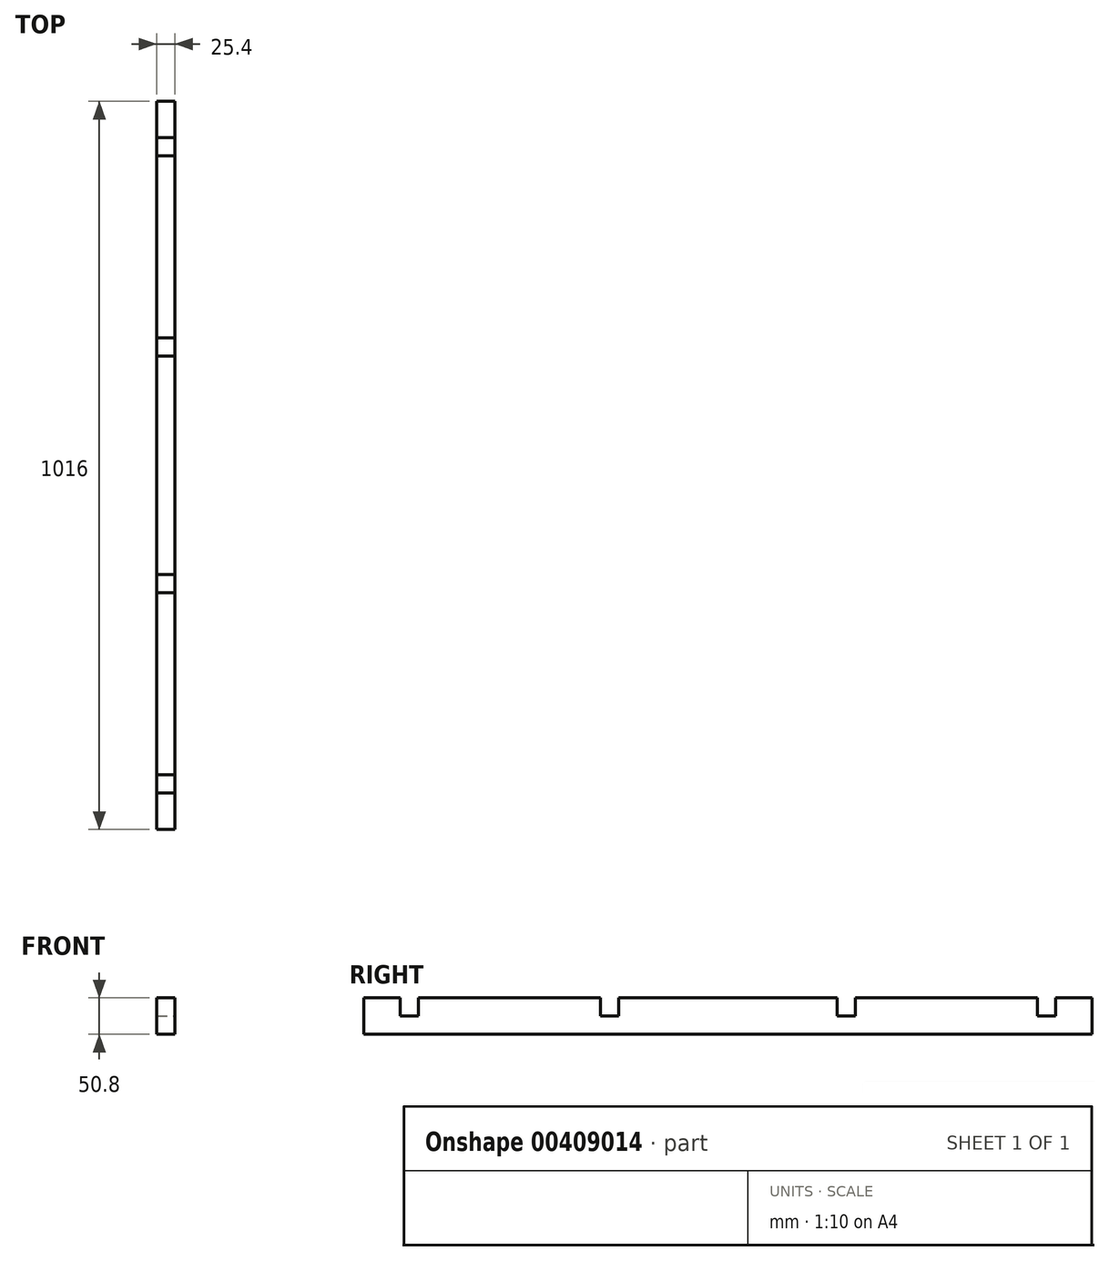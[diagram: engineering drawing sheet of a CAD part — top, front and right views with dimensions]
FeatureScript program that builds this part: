
annotation { "Feature Type Name" : "Feature", "Feature Type Description" : "" }
export const myFeature = defineFeature(function(context is Context, id is Id, definition is map)
    precondition{}
    {
        {
            var Q0;
            Q0=qCreatedBy(makeId("Right.planeOp"),FACE);
            var sketch = newSketch(context, id + "F0", { "sketchPlane" : qUnion([Q0])});
            skLineSegment(sketch, "E0.bottom", {"start": v(-508, 25.4) * mm, "end": v(508, 25.4) * mm});
            skLineSegment(sketch, "E0.top", {"start": v(-508, -25.4) * mm, "end": v(508, -25.4) * mm});
            skLineSegment(sketch, "E0.left", {"start": v(-508, 25.4) * mm, "end": v(-508, -25.4) * mm});
            skLineSegment(sketch, "E0.right", {"start": v(508, 25.4) * mm, "end": v(508, -25.4) * mm});
            skPoint(sketch, "E0.middle", {"position": v(0, 0) * mm});
            skSolve(sketch);
        }
        {
            var Q0;
            Q0=makeQuery(id+"F0.imprint","IMPRINT",FACE,{"disambiguationData":[TD([[makeQuery(id+"F0.imprint","IMPRINT",EDGE,{"derivedFrom":sQuery(id+"F0.wireOp",EDGE,"E0.bottom")}),-1.0]])]});
            extrude(context, id + "F1", {"entities" : qUnion([Q0]), "depth" : 25.4 * mm});
        }
        {
            var Q0;
            Q0=makeQuery(id+"F1.opExtrude","CAP_FACE",FACE,{"disambiguationData":[OSD([sQuery(id+"F0.wireOp",EDGE,"E0.bottom"),sQuery(id+"F0.wireOp",EDGE,"E0.top"),sQuery(id+"F0.wireOp",EDGE,"E0.left"),sQuery(id+"F0.wireOp",EDGE,"E0.right")])],"isStart":false});
            var sketch = newSketch(context, id + "F2", { "sketchPlane" : qUnion([Q0])});
            skLineSegment(sketch, "E1.bottom", {"start": v(-152.4, 0) * mm, "end": v(-177.8, 0) * mm});
            skLineSegment(sketch, "E1.top", {"start": v(-152.4, 25.4) * mm, "end": v(-177.8, 25.4) * mm});
            skLineSegment(sketch, "E1.left", {"start": v(-152.4, 0) * mm, "end": v(-152.4, 25.4) * mm});
            skLineSegment(sketch, "E1.right", {"start": v(-177.8, 0) * mm, "end": v(-177.8, 25.4) * mm});
            skLineSegment(sketch, "E2.bottom", {"start": v(152.4, 0) * mm, "end": v(177.8, 0) * mm});
            skLineSegment(sketch, "E2.top", {"start": v(152.4, 25.4) * mm, "end": v(177.8, 25.4) * mm});
            skLineSegment(sketch, "E2.left", {"start": v(152.4, 0) * mm, "end": v(152.4, 25.4) * mm});
            skLineSegment(sketch, "E2.right", {"start": v(177.8, 0) * mm, "end": v(177.8, 25.4) * mm});
            skSolve(sketch);
        }
        {
            var Q0;
            Q0 = qSketchRegion(id + "F2", true);
            extrude(context, id + "F3", {"entities" : qUnion([Q0]), "operationType" : NewBodyOperationType.REMOVE, "oppositeDirection" : true, "depth" : 25.4 * mm});
        }
        {
            var Q0;
            Q0=makeQuery(id+"F1.opExtrude","CAP_FACE",FACE,{"disambiguationData":[OSD([sQuery(id+"F0.wireOp",EDGE,"E0.bottom"),sQuery(id+"F0.wireOp",EDGE,"E0.top"),sQuery(id+"F0.wireOp",EDGE,"E0.left"),sQuery(id+"F0.wireOp",EDGE,"E0.right")])],"isStart":false});
            var sketch = newSketch(context, id + "F4", { "sketchPlane" : qUnion([Q0])});
            skPoint(sketch, "E3.endSnap0", {"position": v(-508, 0) * mm});
            skLineSegment(sketch, "E4.bottom", {"start": v(-457.2, 0) * mm, "end": v(-431.8, 0) * mm});
            skLineSegment(sketch, "E4.top", {"start": v(-457.2, 25.4) * mm, "end": v(-431.8, 25.4) * mm});
            skLineSegment(sketch, "E4.left", {"start": v(-457.2, 0) * mm, "end": v(-457.2, 25.4) * mm});
            skLineSegment(sketch, "E4.right", {"start": v(-431.8, 0) * mm, "end": v(-431.8, 25.4) * mm});
            skPoint(sketch, "E5.endSnap0", {"position": v(508, 0) * mm});
            skLineSegment(sketch, "E6.bottom", {"start": v(457.2, 0) * mm, "end": v(431.8, 0) * mm});
            skLineSegment(sketch, "E6.top", {"start": v(457.2, 25.4) * mm, "end": v(431.8, 25.4) * mm});
            skLineSegment(sketch, "E6.left", {"start": v(457.2, 0) * mm, "end": v(457.2, 25.4) * mm});
            skLineSegment(sketch, "E6.right", {"start": v(431.8, 0) * mm, "end": v(431.8, 25.4) * mm});
            skSolve(sketch);
        }
        {
            var Q0;
            Q0 = qSketchRegion(id + "F4", true);
            extrude(context, id + "F5", {"entities" : qUnion([Q0]), "operationType" : NewBodyOperationType.REMOVE, "oppositeDirection" : true, "depth" : 25.4 * mm});
        }
    });
